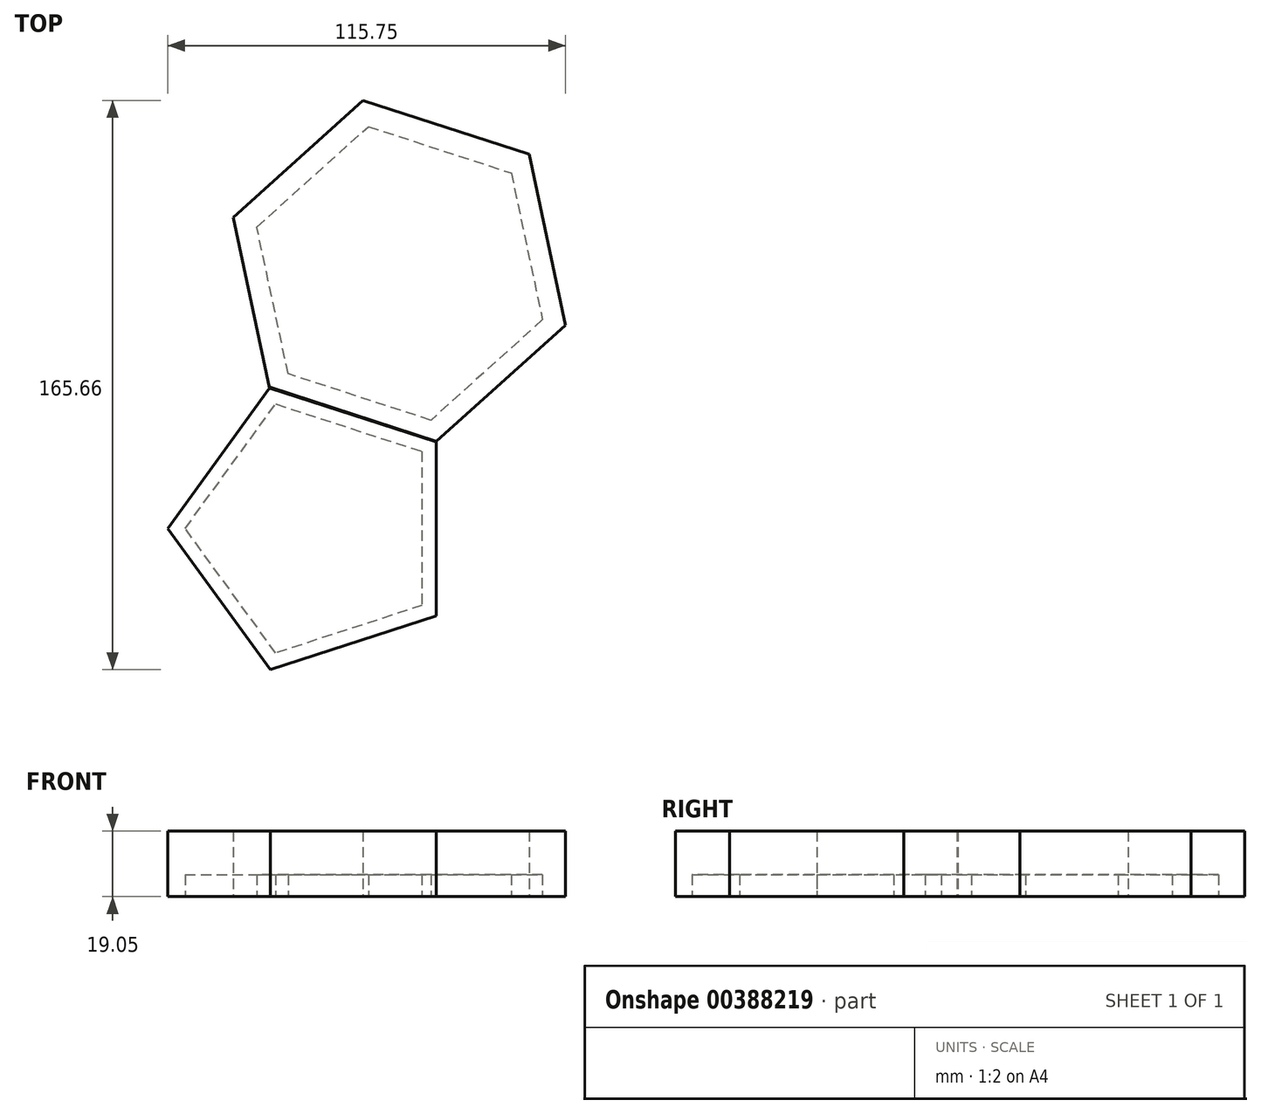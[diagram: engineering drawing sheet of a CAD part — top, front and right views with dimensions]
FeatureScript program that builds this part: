
annotation { "Feature Type Name" : "Feature", "Feature Type Description" : "" }
export const myFeature = defineFeature(function(context is Context, id is Id, definition is map)
    precondition{}
    {
        {
            var Q0;
            Q0=qCreatedBy(makeId("Top.planeOp"),FACE);
            var sketch = newSketch(context, id + "F0", { "sketchPlane" : qUnion([Q0])});
            skCircle(sketch, "E0.cCircle", {"center": v(0, 0) * mm, "radius": 43.21 * mm, "construction": true});
            skLineSegment(sketch, "E0.0", {"start": v(34.96, 25.4) * mm, "end": v(34.96, -25.4) * mm});
            skLineSegment(sketch, "E0.1", {"start": v(34.96, -25.4) * mm, "end": v(-13.35, -41.1) * mm});
            skLineSegment(sketch, "E0.2", {"start": v(-13.35, -41.1) * mm, "end": v(-43.21, 0) * mm});
            skLineSegment(sketch, "E0.3", {"start": v(-43.21, 0) * mm, "end": v(-13.35, 41.1) * mm});
            skLineSegment(sketch, "E0.4", {"start": v(-13.35, 41.1) * mm, "end": v(34.96, 25.4) * mm});
            skCircle(sketch, "E1.cCircle", {"center": v(24.22, 74.87) * mm, "radius": 50.8 * mm, "construction": true});
            skLineSegment(sketch, "E1.0", {"start": v(-24.1, 90.57) * mm, "end": v(13.66, 124.56) * mm});
            skLineSegment(sketch, "E1.1", {"start": v(13.66, 124.56) * mm, "end": v(61.97, 108.87) * mm});
            skLineSegment(sketch, "E1.2", {"start": v(61.97, 108.87) * mm, "end": v(72.54, 59.18) * mm});
            skLineSegment(sketch, "E1.3", {"start": v(72.54, 59.18) * mm, "end": v(34.78, 25.18) * mm});
            skLineSegment(sketch, "E1.4", {"start": v(34.78, 25.18) * mm, "end": v(-13.53, 40.88) * mm});
            skLineSegment(sketch, "E1.5", {"start": v(-13.53, 40.88) * mm, "end": v(-24.1, 90.57) * mm});
            skSolve(sketch);
        }
        {
            var Q0;
            {var subQ4=sQuery(id+"F0.wireOp",EDGE,"E0.1");Q0=makeQuery(id+"F0.imprint","IMPRINT",FACE,{"disambiguationData":[TD([[makeQuery(id+"F0.imprint","IMPRINT",EDGE,{"derivedFrom":subQ4}),-1.0]])]});}
            var Q1;
            {var subQ0=sQuery(id+"F0.wireOp",EDGE,"E0.4");Q1=makeQuery(id+"F0.imprint","IMPRINT",FACE,{"disambiguationData":[TD([[makeQuery(id+"F0.imprint","IMPRINT",EDGE,{"derivedFrom":subQ0}),1.0]])]});}
            extrude(context, id + "F1", {"entities" : qUnion([Q0, Q1]), "depth" : 19.05 * mm});
        }
        {
            var Q0;
            Q0=qCreatedBy(makeId("Top.planeOp"),FACE);
            var sketch = newSketch(context, id + "F2", { "sketchPlane" : qUnion([Q0])});
            skCircle(sketch, "E2.cCircle", {"center": v(0, 0) * mm, "radius": 38.1 * mm, "construction": true});
            skLineSegment(sketch, "E2.0", {"start": v(-11.77, 36.24) * mm, "end": v(30.82, 22.4) * mm});
            skLineSegment(sketch, "E2.1", {"start": v(30.82, 22.4) * mm, "end": v(30.82, -22.4) * mm});
            skLineSegment(sketch, "E2.2", {"start": v(30.82, -22.4) * mm, "end": v(-11.77, -36.24) * mm});
            skLineSegment(sketch, "E2.3", {"start": v(-11.77, -36.24) * mm, "end": v(-38.1, 0) * mm});
            skLineSegment(sketch, "E2.4", {"start": v(-38.1, 0) * mm, "end": v(-11.77, 36.24) * mm});
            skCircle(sketch, "E3.cCircle", {"center": v(24.31, 74.23) * mm, "radius": 43.68 * mm, "construction": true});
            skLineSegment(sketch, "E3.0", {"start": v(56.77, 103.46) * mm, "end": v(65.86, 60.73) * mm});
            skLineSegment(sketch, "E3.1", {"start": v(65.86, 60.73) * mm, "end": v(33.4, 31.5) * mm});
            skLineSegment(sketch, "E3.2", {"start": v(33.4, 31.5) * mm, "end": v(-8.15, 45) * mm});
            skLineSegment(sketch, "E3.3", {"start": v(-8.15, 45) * mm, "end": v(-17.23, 87.73) * mm});
            skLineSegment(sketch, "E3.4", {"start": v(-17.23, 87.73) * mm, "end": v(15.23, 116.95) * mm});
            skLineSegment(sketch, "E3.5", {"start": v(15.23, 116.95) * mm, "end": v(56.77, 103.46) * mm});
            skSolve(sketch);
        }
        {
            var Q0;
            Q0 = qSketchRegion(id + "F2", true);
            extrude(context, id + "F3", {"entities" : qUnion([Q0]), "depth" : 6.35 * mm});
        }
    });
